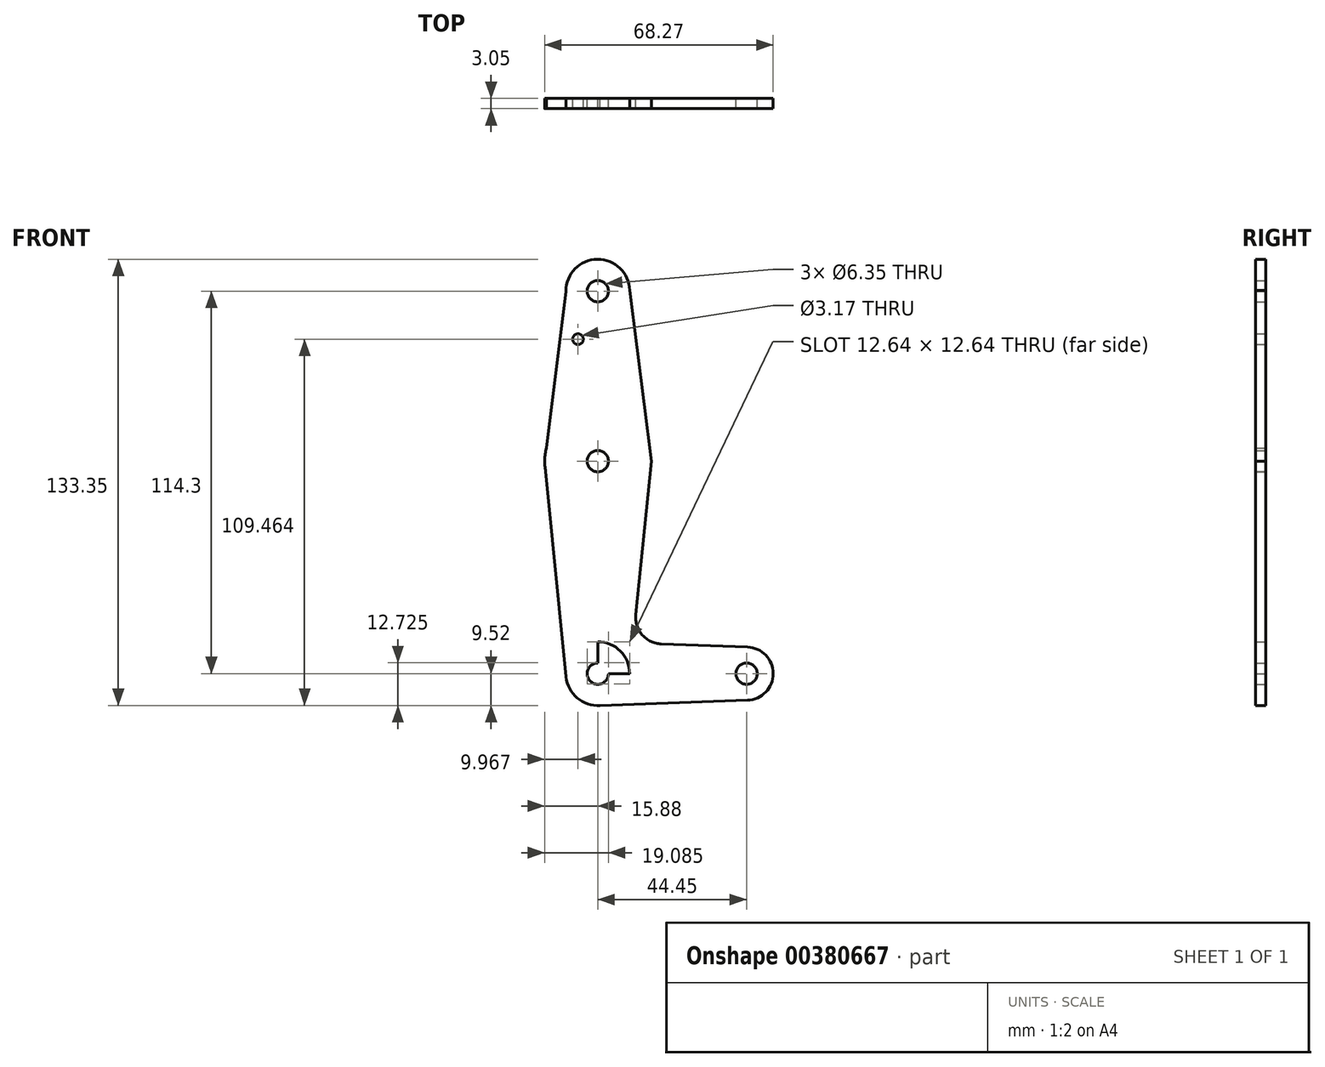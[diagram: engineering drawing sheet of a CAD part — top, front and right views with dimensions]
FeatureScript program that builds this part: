
annotation { "Feature Type Name" : "Feature", "Feature Type Description" : "" }
export const myFeature = defineFeature(function(context is Context, id is Id, definition is map)
    precondition{}
    {
        {
            var Q0;
            Q0=qCreatedBy(makeId("Front.planeOp"),FACE);
            var sketch = newSketch(context, id + "F0", { "sketchPlane" : qUnion([Q0])});
            skLineSegment(sketch, "E0", {"start": v(0, 55.88) * mm, "end": v(0, -58.42) * mm});
            skCircle(sketch, "E1", {"center": v(0, 55.88) * mm, "radius": 9.53 * mm});
            skCircle(sketch, "E2", {"center": v(0, -58.42) * mm, "radius": 9.53 * mm});
            skLineSegment(sketch, "E3", {"start": v(0, -58.42) * mm, "end": v(0, 5.08) * mm});
            skCircle(sketch, "E4", {"center": v(0, 5.08) * mm, "radius": 15.88 * mm});
            skLineSegment(sketch, "E5", {"start": v(0, -58.42) * mm, "end": v(44.45, -58.42) * mm});
            skCircle(sketch, "E6", {"center": v(44.45, -58.42) * mm, "radius": 7.94 * mm});
            skLineSegment(sketch, "E7", {"start": v(-9.52, 55.88) * mm, "end": v(-15.87, 5.08) * mm});
            skLineSegment(sketch, "E8", {"start": v(9.52, 56.14) * mm, "end": v(16, 5.08) * mm});
            skLineSegment(sketch, "E9", {"start": v(-15.87, 5.08) * mm, "end": v(-9.48, -59.36) * mm});
            skLineSegment(sketch, "E10", {"start": v(16, 5.08) * mm, "end": v(11.36, -40.82) * mm});
            skLineSegment(sketch, "E11", {"start": v(0, -67.94) * mm, "end": v(44.73, -66.35) * mm});
            skLineSegment(sketch, "E12", {"start": v(18.98, -49.57) * mm, "end": v(44.73, -50.49) * mm});
            skCircle(sketch, "E13", {"center": v(0, 55.88) * mm, "radius": 3.18 * mm});
            skCircle(sketch, "E14", {"center": v(0, 5.08) * mm, "radius": 3.18 * mm});
            skCircle(sketch, "E15", {"center": v(0, -58.42) * mm, "radius": 3.18 * mm});
            skCircle(sketch, "E16", {"center": v(44.45, -58.42) * mm, "radius": 3.18 * mm});
            skLineSegment(sketch, "E17", {"start": v(0, 5.08) * mm, "end": v(0, 41.6) * mm});
            skArc(sketch, "E18.filletArc", {"start": v(11.36, -40.82) * mm, "mid": v(13.27, -46.85) * mm, "end": v(18.98, -49.57) * mm});
            skCircle(sketch, "E19", {"center": v(-5.91, 41.52) * mm, "radius": 1.59 * mm});
            skSolve(sketch);
        }
        {
            var Q0;
            Q0 = qSketchRegion(id + "F0", true);
            var Q1;
            {var subQ0=sQuery(id+"F0.wireOp",EDGE,"E3");var subQ1=sQuery(id+"F0.wireOp",EDGE,"E2");var subQ2=makeQuery(id+"F0.imprint","INTERSECT",VERTEX,{"derivedFrom":[subQ1,subQ0]});Q1=makeQuery(id+"F0.imprint","IMPRINT",FACE,{"disambiguationData":[TD([[makeQuery(id+"F0.imprint","IMPRINT",EDGE,{"disambiguationData":[TD([[subQ2,1.0]])],"derivedFrom":subQ1}),1.0]])]});}
            extrude(context, id + "F1", {"entities" : qUnion([Q0, Q1]), "depth" : 3.05 * mm});
        }
    });
